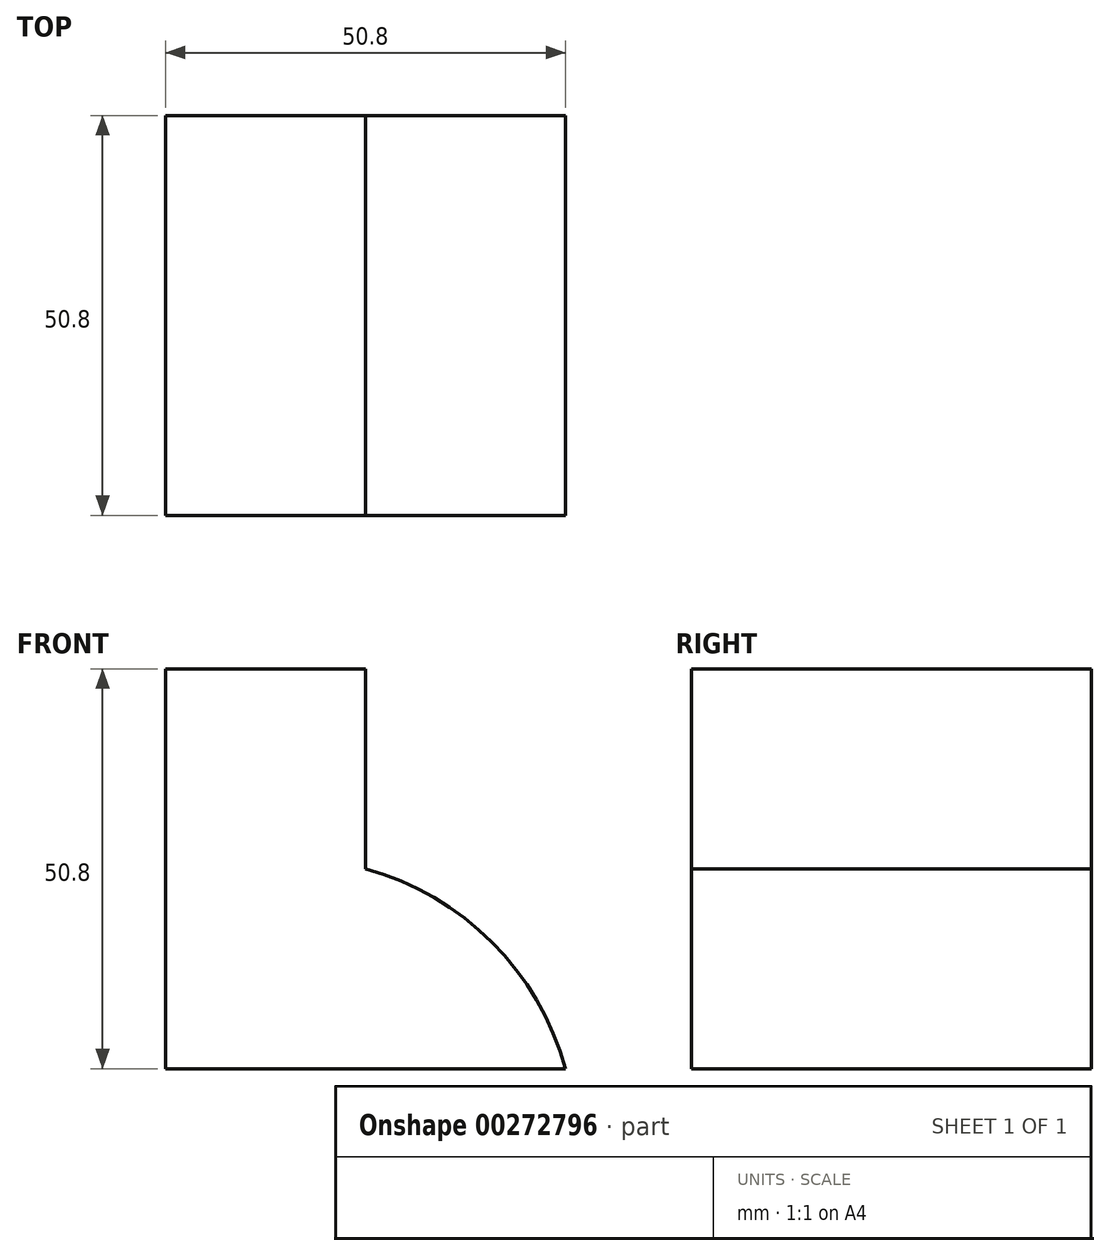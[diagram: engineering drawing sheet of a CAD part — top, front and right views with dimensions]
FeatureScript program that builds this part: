
annotation { "Feature Type Name" : "Feature", "Feature Type Description" : "" }
export const myFeature = defineFeature(function(context is Context, id is Id, definition is map)
    precondition{}
    {
        {
            var Q0;
            Q0=qCreatedBy(makeId("Front.planeOp"),FACE);
            var sketch = newSketch(context, id + "F0", { "sketchPlane" : qUnion([Q0])});
            skLineSegment(sketch, "E0", {"start": v(0, 0) * mm, "end": v(-50.8, 0) * mm});
            skLineSegment(sketch, "E1", {"start": v(-50.8, 0) * mm, "end": v(-50.8, 50.8) * mm});
            skLineSegment(sketch, "E2", {"start": v(-50.8, 50.8) * mm, "end": v(-25.4, 50.8) * mm});
            skLineSegment(sketch, "E3", {"start": v(-25.4, 50.8) * mm, "end": v(-25.4, 25.4) * mm});
            skArc(sketch, "E4", {"start": v(0, 0) * mm, "mid": v(-9.34, 16.06) * mm, "end": v(-25.4, 25.4) * mm});
            skSolve(sketch);
        }
        {
            var Q0;
            Q0 = qSketchRegion(id + "F0", true);
            extrude(context, id + "F1", {"entities" : qUnion([Q0]), "depth" : 50.8 * mm});
        }
    });
